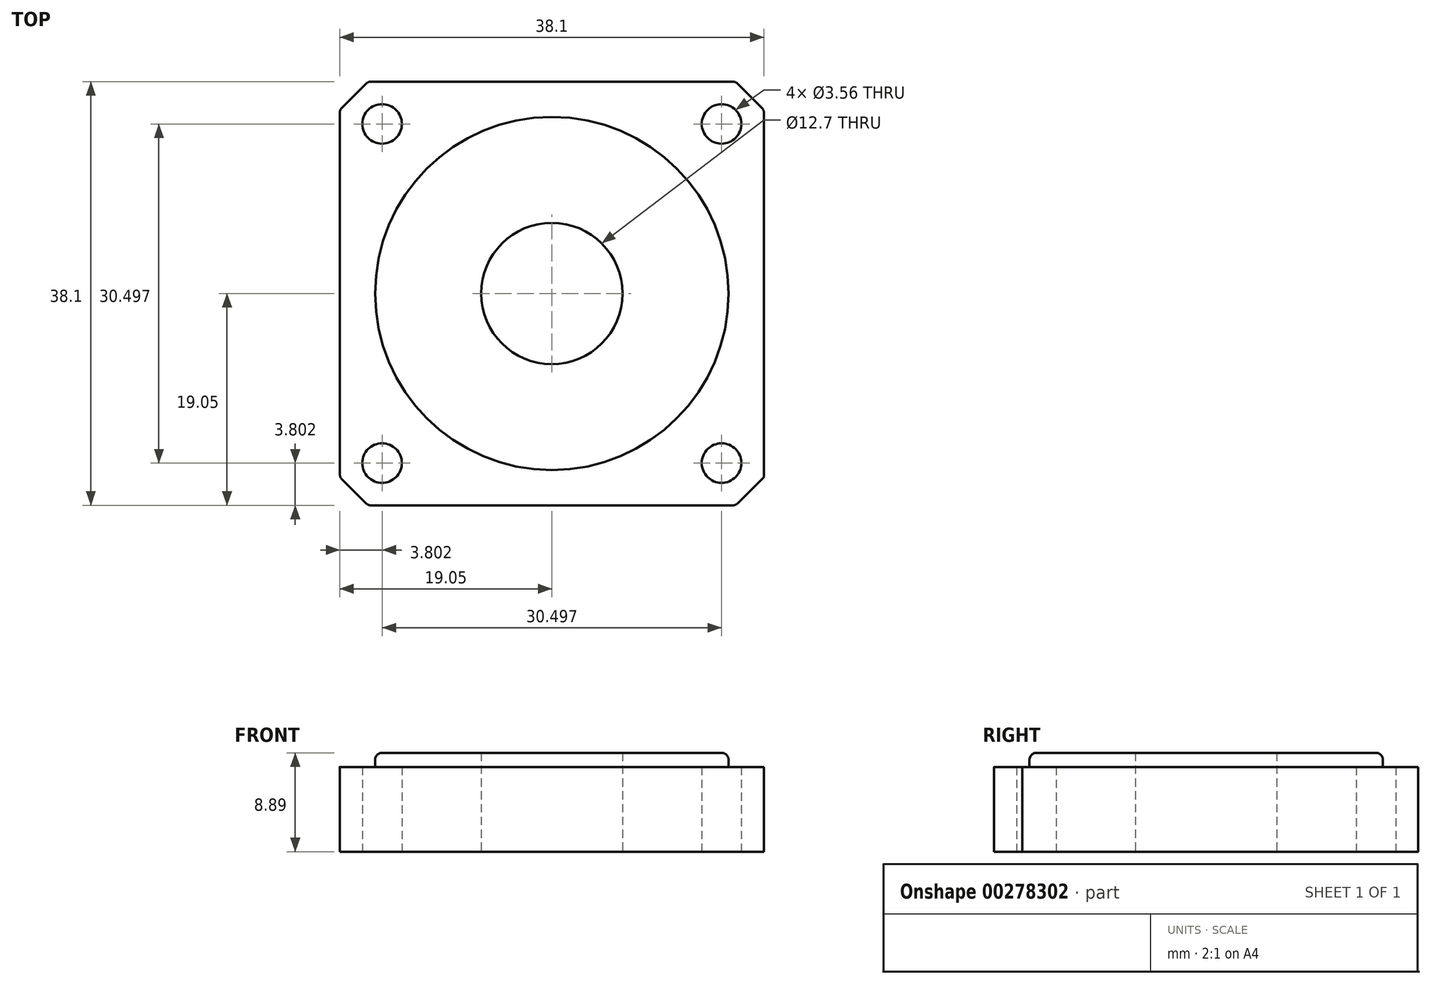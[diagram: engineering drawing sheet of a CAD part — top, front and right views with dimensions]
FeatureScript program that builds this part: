
annotation { "Feature Type Name" : "Feature", "Feature Type Description" : "" }
export const myFeature = defineFeature(function(context is Context, id is Id, definition is map)
    precondition{}
    {
        {
            var Q0;
            Q0=qCreatedBy(makeId("Top.planeOp"),FACE);
            var sketch = newSketch(context, id + "F0", { "sketchPlane" : qUnion([Q0])});
            skLineSegment(sketch, "E0.bottom", {"start": v(-19.05, 19.05) * mm, "end": v(19.05, 19.05) * mm});
            skLineSegment(sketch, "E0.top", {"start": v(-19.05, -19.05) * mm, "end": v(19.05, -19.05) * mm});
            skLineSegment(sketch, "E0.left", {"start": v(-19.05, 19.05) * mm, "end": v(-19.05, -19.05) * mm});
            skLineSegment(sketch, "E0.right", {"start": v(19.05, 19.05) * mm, "end": v(19.05, -19.05) * mm});
            skPoint(sketch, "E0.middle", {"position": v(0, 0) * mm});
            skCircle(sketch, "E1", {"center": v(0, 0) * mm, "radius": 6.35 * mm});
            skLineSegment(sketch, "E2", {"start": v(0, 0) * mm, "end": v(19.05, 0) * mm});
            skLineSegment(sketch, "E3", {"start": v(0, 0) * mm, "end": v(15.25, -15.25) * mm});
            skLineSegment(sketch, "E4", {"start": v(0, 0) * mm, "end": v(-15.25, -15.25) * mm});
            skLineSegment(sketch, "E5", {"start": v(0, 0) * mm, "end": v(-15.25, 15.25) * mm});
            skLineSegment(sketch, "E6", {"start": v(0, 0) * mm, "end": v(15.25, 15.25) * mm});
            skCircle(sketch, "E7", {"center": v(-15.25, -15.25) * mm, "radius": 1.78 * mm});
            skCircle(sketch, "E8", {"center": v(-15.25, 15.25) * mm, "radius": 1.78 * mm});
            skCircle(sketch, "E9", {"center": v(15.25, 15.25) * mm, "radius": 1.78 * mm});
            skCircle(sketch, "E10", {"center": v(15.25, -15.25) * mm, "radius": 1.78 * mm});
            skLineSegment(sketch, "E11", {"start": v(-19.05, 19.05) * mm, "end": v(-19.05, 16.51) * mm});
            skLineSegment(sketch, "E12", {"start": v(-19.05, 16.51) * mm, "end": v(-16.51, 19.05) * mm});
            skLineSegment(sketch, "E13", {"start": v(19.05, 16.51) * mm, "end": v(16.51, 19.05) * mm});
            skLineSegment(sketch, "E14", {"start": v(16.51, -19.05) * mm, "end": v(19.05, -16.51) * mm});
            skLineSegment(sketch, "E15", {"start": v(-16.51, -19.05) * mm, "end": v(-19.05, -16.51) * mm});
            skSolve(sketch);
        }
        {
            var Q0;
            Q0=makeQuery(id+"F0.imprint","IMPRINT",FACE,{"disambiguationData":[TD([[makeQuery(id+"F0.imprint","IMPRINT",EDGE,{"derivedFrom":sQuery(id+"F0.wireOp",EDGE,"E7")}),-1.0]])]});
            extrude(context, id + "F1", {"entities" : qUnion([Q0]), "depth" : 7.62 * mm});
        }
        {
            var Q0;
            Q0=makeQuery(id+"F1.opExtrude","CAP_FACE",FACE,{"disambiguationData":[OSD([sQuery(id+"F0.wireOp",EDGE,"E0.bottom"),sQuery(id+"F0.wireOp",EDGE,"E0.top"),sQuery(id+"F0.wireOp",EDGE,"E0.left"),sQuery(id+"F0.wireOp",EDGE,"E0.right"),sQuery(id+"F0.wireOp",EDGE,"E1"),sQuery(id+"F0.wireOp",EDGE,"E7"),sQuery(id+"F0.wireOp",EDGE,"E8"),sQuery(id+"F0.wireOp",EDGE,"E9"),sQuery(id+"F0.wireOp",EDGE,"E10")])],"isStart":false});
            var sketch = newSketch(context, id + "F2", { "sketchPlane" : qUnion([Q0])});
            skCircle(sketch, "E16", {"center": v(0, 0) * mm, "radius": 15.88 * mm});
            skSolve(sketch);
        }
        {
            var Q0;
            Q0=makeQuery(id+"F2.imprint","IMPRINT",FACE,{"disambiguationData":[TD([[makeQuery(id+"F2.imprint","IMPRINT",EDGE,{"derivedFrom":sQuery(id+"F2.wireOp",EDGE,"E16")}),1.0]])]});
            extrude(context, id + "F3", {"entities" : qUnion([Q0]), "operationType" : NewBodyOperationType.ADD, "depth" : 1.27 * mm});
        }
        {
            var Q0;
            Q0=makeQuery(id+"F3.opExtrude","CAP_EDGE",EDGE,{"disambiguationData":[OSD([sQuery(id+"F2.wireOp",EDGE,"E16")])],"isStart":false});
            var Q1;
            Q1=makeQuery(id+"F1.opExtrude","SWEPT_EDGE",EDGE,{"disambiguationData":[OSD([sQuery(id+"F0.wireOp",EDGE,"E0.left"),sQuery(id+"F0.wireOp",EDGE,"E11"),sQuery(id+"F0.wireOp",EDGE,"E12")])]});
            var Q2;
            Q2=makeQuery(id+"F1.opExtrude","SWEPT_EDGE",EDGE,{"disambiguationData":[OSD([sQuery(id+"F0.wireOp",EDGE,"E0.left"),sQuery(id+"F0.wireOp",EDGE,"E15")])]});
            var Q3;
            Q3=makeQuery(id+"F1.opExtrude","SWEPT_EDGE",EDGE,{"disambiguationData":[OSD([sQuery(id+"F0.wireOp",EDGE,"E0.top"),sQuery(id+"F0.wireOp",EDGE,"E15")])]});
            var Q4;
            Q4=makeQuery(id+"F1.opExtrude","SWEPT_EDGE",EDGE,{"disambiguationData":[OSD([sQuery(id+"F0.wireOp",EDGE,"E0.top"),sQuery(id+"F0.wireOp",EDGE,"E14")])]});
            var Q5;
            Q5=makeQuery(id+"F1.opExtrude","SWEPT_EDGE",EDGE,{"disambiguationData":[OSD([sQuery(id+"F0.wireOp",EDGE,"E0.right"),sQuery(id+"F0.wireOp",EDGE,"E13")])]});
            var Q6;
            Q6=makeQuery(id+"F1.opExtrude","SWEPT_EDGE",EDGE,{"disambiguationData":[OSD([sQuery(id+"F0.wireOp",EDGE,"E0.bottom"),sQuery(id+"F0.wireOp",EDGE,"E13")])]});
            var Q7;
            Q7=makeQuery(id+"F1.opExtrude","SWEPT_EDGE",EDGE,{"disambiguationData":[OSD([sQuery(id+"F0.wireOp",EDGE,"E0.bottom"),sQuery(id+"F0.wireOp",EDGE,"E12")])]});
            fillet(context, id + "F4", {"entities" : qUnion([Q0, Q1, Q2, Q3, Q4, Q5, Q6, Q7]), "radius" : 0.64 * mm, "tangentPropagation" : true, "allowEdgeOverflow" : false});
        }
    });
